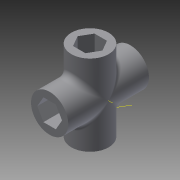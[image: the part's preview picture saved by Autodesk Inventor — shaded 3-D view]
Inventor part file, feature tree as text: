
AUTODESK INVENTOR PART (.ipt)
format: ipt  version: 2015 SP1 (Build 190203100, 203)  size: 244,224 bytes
history: native  units: mm
features: other x4, extrude x4, sketch x4, projected_geometry x2, pattern_circular x1, fillet x1
ambient origin geometry x8: Origin, YZ Plane, XZ Plane, XY Plane, X Axis, Y Axis, Z Axis, Center Point
bodies: Body1 (feature_tree)
feature tree (16):
  other  "Sólido1"
  extrude  "Extrusión1"  Depth=12.0mm
  extrude  "Extrusión2"  Depth=6.0mm TaperAngle=0.0deg
  other  "Eje de trabajo1"
  other  "Eje de trabajo2"
  pattern_circular  "Patrón circular3"  Count=4 Angle=360.0deg
  extrude  "Extrusión6"  Depth=245.0mm TaperAngle=0.0deg
  extrude  "Extrusión7"  [1 undecoded]
  fillet  "Empalme2"  [1 undecoded]
  sketch  "Boceto1"  dims[d0=8.0mm d1=12.0mm]
  sketch  "Boceto2"  dims[d2=7.0mm d3=0.0mm d4=6.0mm d5=0.0mm d19=40.0mm d20=360.0deg]
  other  "Punto de trabajo1"
  sketch  "Boceto7"  dims[d22=245.0mm d23=0.0mm d24=245.0mm d25=0.0mm]
  projected_geometry  "Contorno proyectado5"
  sketch  "Boceto8"  dims[d26=2.0mm]
  projected_geometry  "Contorno proyectado6"
note: 2 required parameter values undecoded (feature->parameter linkage not recoverable at this tier; creation-order binding heuristic only, values carry confidence <= 0.55)
